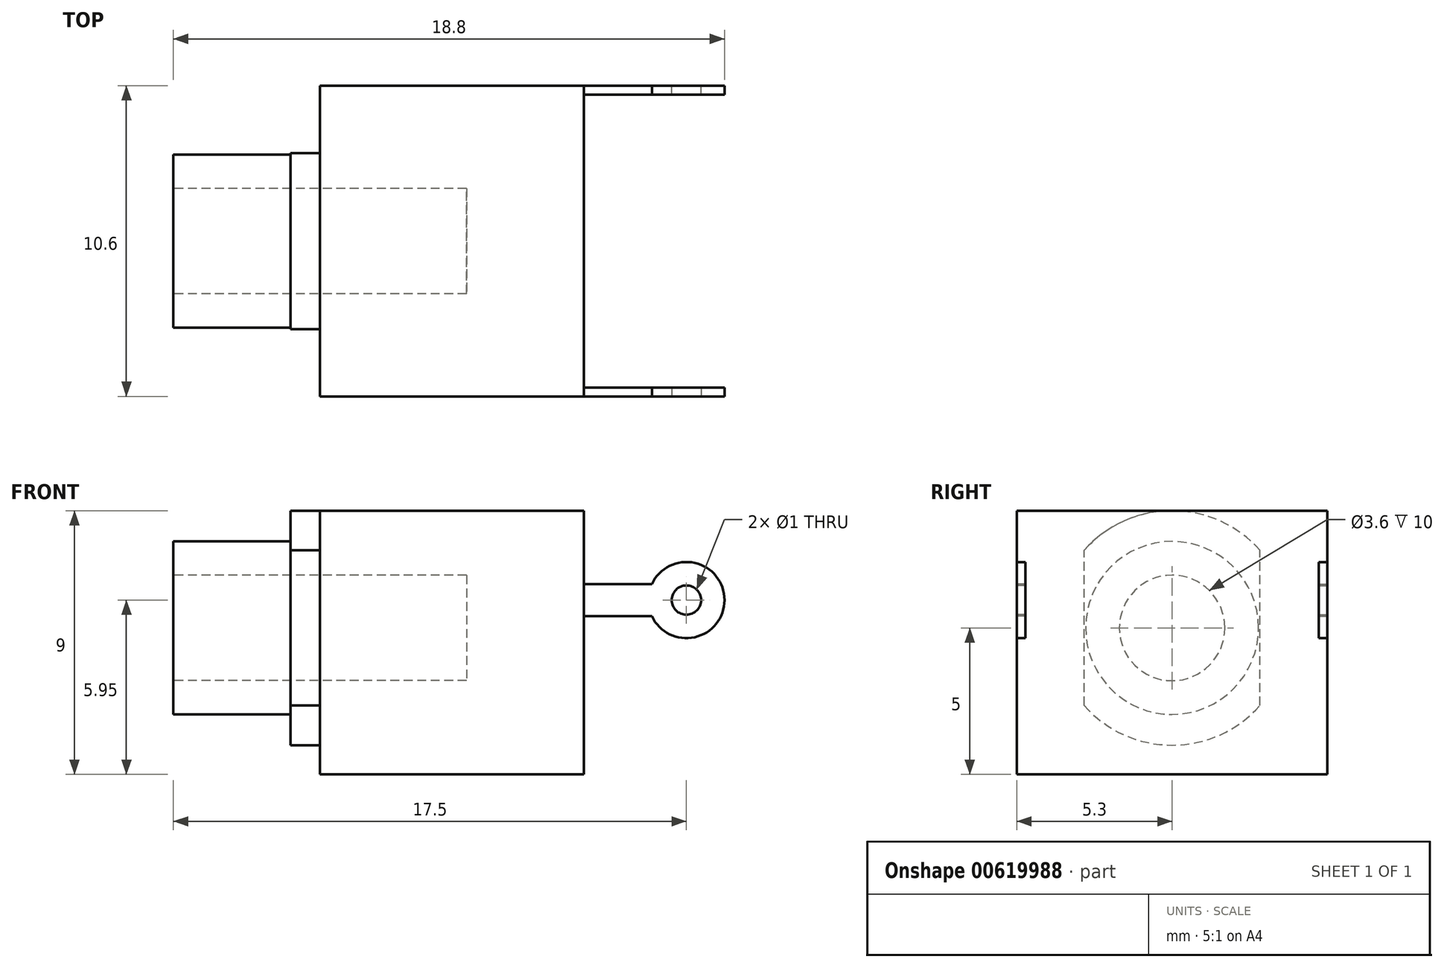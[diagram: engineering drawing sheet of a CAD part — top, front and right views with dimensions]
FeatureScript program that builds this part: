
annotation { "Feature Type Name" : "Feature", "Feature Type Description" : "" }
export const myFeature = defineFeature(function(context is Context, id is Id, definition is map)
    precondition{}
    {
        {
            var Q0;
            Q0=qCreatedBy(makeId("Top.planeOp"),FACE);
            var sketch = newSketch(context, id + "F0", { "sketchPlane" : qUnion([Q0])});
            skLineSegment(sketch, "E0.bottom", {"start": v(4.5, 5.3) * mm, "end": v(-4.5, 5.3) * mm});
            skLineSegment(sketch, "E0.top", {"start": v(4.5, -5.3) * mm, "end": v(-4.5, -5.3) * mm});
            skLineSegment(sketch, "E0.left", {"start": v(4.5, 5.3) * mm, "end": v(4.5, -5.3) * mm});
            skLineSegment(sketch, "E0.right", {"start": v(-4.5, 5.3) * mm, "end": v(-4.5, -5.3) * mm});
            skPoint(sketch, "E0.middle", {"position": v(0, 0) * mm});
            skSolve(sketch);
        }
        {
            var Q0;
            Q0 = qSketchRegion(id + "F0", true);
            extrude(context, id + "F1", {"entities" : qUnion([Q0]), "depth" : 9 * mm, "offsetDistance" : 25 * mm});
        }
        {
            var Q0;
            Q0=makeQuery(id+"F1.opExtrude","SWEPT_FACE",FACE,{"disambiguationData":[OSD([sQuery(id+"F0.wireOp",EDGE,"E0.right")])]});
            var sketch = newSketch(context, id + "F2", { "sketchPlane" : qUnion([Q0])});
            skArc(sketch, "E1", {"start": v(3, 7.65) * mm, "mid": v(0, 9) * mm, "end": v(-3, 7.65) * mm});
            skPoint(sketch, "E1.centerSnap0", {"position": v(0, 9) * mm});
            skLineSegment(sketch, "E2", {"start": v(3, 2.35) * mm, "end": v(3, 7.65) * mm});
            skLineSegment(sketch, "E3", {"start": v(-3, 2.35) * mm, "end": v(-3, 7.65) * mm});
            skArc(sketch, "E4.trimOffspring", {"start": v(-3, 2.35) * mm, "mid": v(0, 1) * mm, "end": v(3, 2.35) * mm});
            skSolve(sketch);
        }
        {
            var Q0;
            Q0 = qSketchRegion(id + "F2", true);
            extrude(context, id + "F3", {"entities" : qUnion([Q0]), "operationType" : NewBodyOperationType.ADD, "depth" : 1 * mm, "offsetDistance" : 25 * mm});
        }
        {
            var Q0;
            Q0=makeQuery(id+"F3.opExtrude","CAP_FACE",FACE,{"disambiguationData":[OSD([sQuery(id+"F2.wireOp",EDGE,"E1"),sQuery(id+"F2.wireOp",EDGE,"E2"),sQuery(id+"F2.wireOp",EDGE,"E3"),sQuery(id+"F2.wireOp",EDGE,"E4.trimOffspring")])],"isStart":false});
            var sketch = newSketch(context, id + "F4", { "sketchPlane" : qUnion([Q0])});
            skCircle(sketch, "E5", {"center": v(0, 5) * mm, "radius": 2.95 * mm});
            skSolve(sketch);
        }
        {
            var Q0;
            Q0 = qSketchRegion(id + "F4", true);
            extrude(context, id + "F5", {"entities" : qUnion([Q0]), "operationType" : NewBodyOperationType.ADD, "depth" : 4 * mm, "offsetDistance" : 25 * mm});
        }
        {
            var Q0;
            Q0=makeQuery(id+"F1.opExtrude","SWEPT_FACE",FACE,{"disambiguationData":[OSD([sQuery(id+"F0.wireOp",EDGE,"E0.bottom")])]});
            var sketch = newSketch(context, id + "F6", { "sketchPlane" : qUnion([Q0])});
            skLineSegment(sketch, "E6", {"start": v(-4.5, 6.5) * mm, "end": v(-6.82, 6.5) * mm});
            skLineSegment(sketch, "E7", {"start": v(-4.5, 5.4) * mm, "end": v(-6.82, 5.4) * mm});
            skArc(sketch, "E8", {"start": v(-6.82, 6.5) * mm, "mid": v(-9.3, 5.95) * mm, "end": v(-6.82, 5.4) * mm});
            skCircle(sketch, "E9", {"center": v(-8, 5.95) * mm, "radius": 0.5 * mm});
            skLineSegment(sketch, "E10", {"start": v(-4.5, 6.5) * mm, "end": v(-4.5, 5.4) * mm});
            skSolve(sketch);
        }
        {
            var Q0;
            Q0 = qSketchRegion(id + "F6", true);
            extrude(context, id + "F7", {"entities" : qUnion([Q0]), "operationType" : NewBodyOperationType.ADD, "oppositeDirection" : true, "depth" : 0.3 * mm, "offsetDistance" : 25 * mm});
        }
        {
            var Q0;
            Q0=makeQuery(id+"F1.opExtrude","SWEPT_FACE",FACE,{"disambiguationData":[OSD([sQuery(id+"F0.wireOp",EDGE,"E0.top")])]});
            var sketch = newSketch(context, id + "F8", { "sketchPlane" : qUnion([Q0])});
            skLineSegment(sketch, "E11", {"start": v(4.5, 5.4) * mm, "end": v(6.82, 5.4) * mm});
            skLineSegment(sketch, "E12", {"start": v(4.5, 6.5) * mm, "end": v(6.82, 6.5) * mm});
            skArc(sketch, "E13", {"start": v(6.82, 5.4) * mm, "mid": v(9.3, 5.95) * mm, "end": v(6.82, 6.5) * mm});
            skCircle(sketch, "E14", {"center": v(8, 5.95) * mm, "radius": 0.5 * mm});
            skLineSegment(sketch, "E15", {"start": v(4.5, 5.4) * mm, "end": v(4.5, 6.5) * mm});
            skSolve(sketch);
        }
        {
            var Q0;
            Q0 = qSketchRegion(id + "F8", true);
            extrude(context, id + "F9", {"entities" : qUnion([Q0]), "oppositeDirection" : true, "depth" : 0.3 * mm, "offsetDistance" : 25 * mm});
        }
        {
            var Q0;
            Q0=makeQuery(id+"F5.opExtrude","CAP_FACE",FACE,{"disambiguationData":[OSD([sQuery(id+"F4.wireOp",EDGE,"E5")])],"isStart":false});
            var sketch = newSketch(context, id + "F10", { "sketchPlane" : qUnion([Q0])});
            skCircle(sketch, "E16", {"center": v(0, 5) * mm, "radius": 1.8 * mm});
            skSolve(sketch);
        }
        {
            var Q0;
            Q0 = qSketchRegion(id + "F10", true);
            extrude(context, id + "F11", {"entities" : qUnion([Q0]), "operationType" : NewBodyOperationType.REMOVE, "oppositeDirection" : true, "depth" : 10 * mm, "offsetDistance" : 25 * mm});
        }
    });
